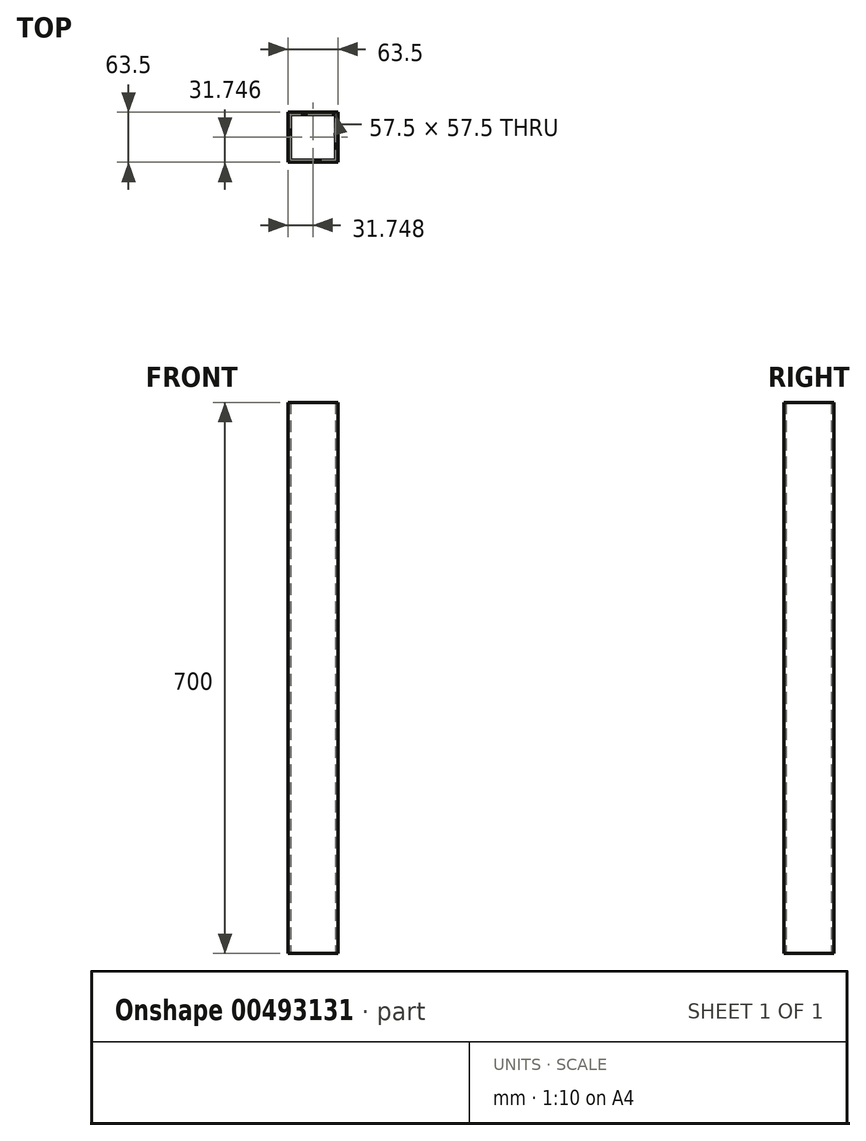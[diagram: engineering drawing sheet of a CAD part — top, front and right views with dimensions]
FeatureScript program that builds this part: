
annotation { "Feature Type Name" : "Feature", "Feature Type Description" : "" }
export const myFeature = defineFeature(function(context is Context, id is Id, definition is map)
    precondition{}
    {
        {
            var Q0;
            Q0=qCreatedBy(makeId("Top.planeOp"),FACE);
            var sketch = newSketch(context, id + "F0", { "sketchPlane" : qUnion([Q0])});
            skLineSegment(sketch, "E0.bottom", {"start": v(-32.2, 11.96) * mm, "end": v(25.3, 11.96) * mm});
            skLineSegment(sketch, "E0.top", {"start": v(-32.2, -45.54) * mm, "end": v(25.3, -45.54) * mm});
            skLineSegment(sketch, "E0.left", {"start": v(-32.2, 11.96) * mm, "end": v(-32.2, -45.54) * mm});
            skLineSegment(sketch, "E0.right", {"start": v(25.3, 11.96) * mm, "end": v(25.3, -45.54) * mm});
            skLineSegment(sketch, "E1.bottom", {"start": v(-35.2, 14.96) * mm, "end": v(28.3, 14.96) * mm});
            skLineSegment(sketch, "E1.top", {"start": v(-35.2, -48.54) * mm, "end": v(28.3, -48.54) * mm});
            skLineSegment(sketch, "E1.left", {"start": v(-35.2, 14.96) * mm, "end": v(-35.2, -48.54) * mm});
            skLineSegment(sketch, "E1.right", {"start": v(28.3, 14.96) * mm, "end": v(28.3, -48.54) * mm});
            skSolve(sketch);
        }
        {
            var Q0;
            Q0=qSketchRegion(id+"F0",true);
            extrude(context, id + "F1", {"entities" : qUnion([Q0]), "offsetDistance" : 25 * mm, "depth" : 700 * mm});
        }
    });
